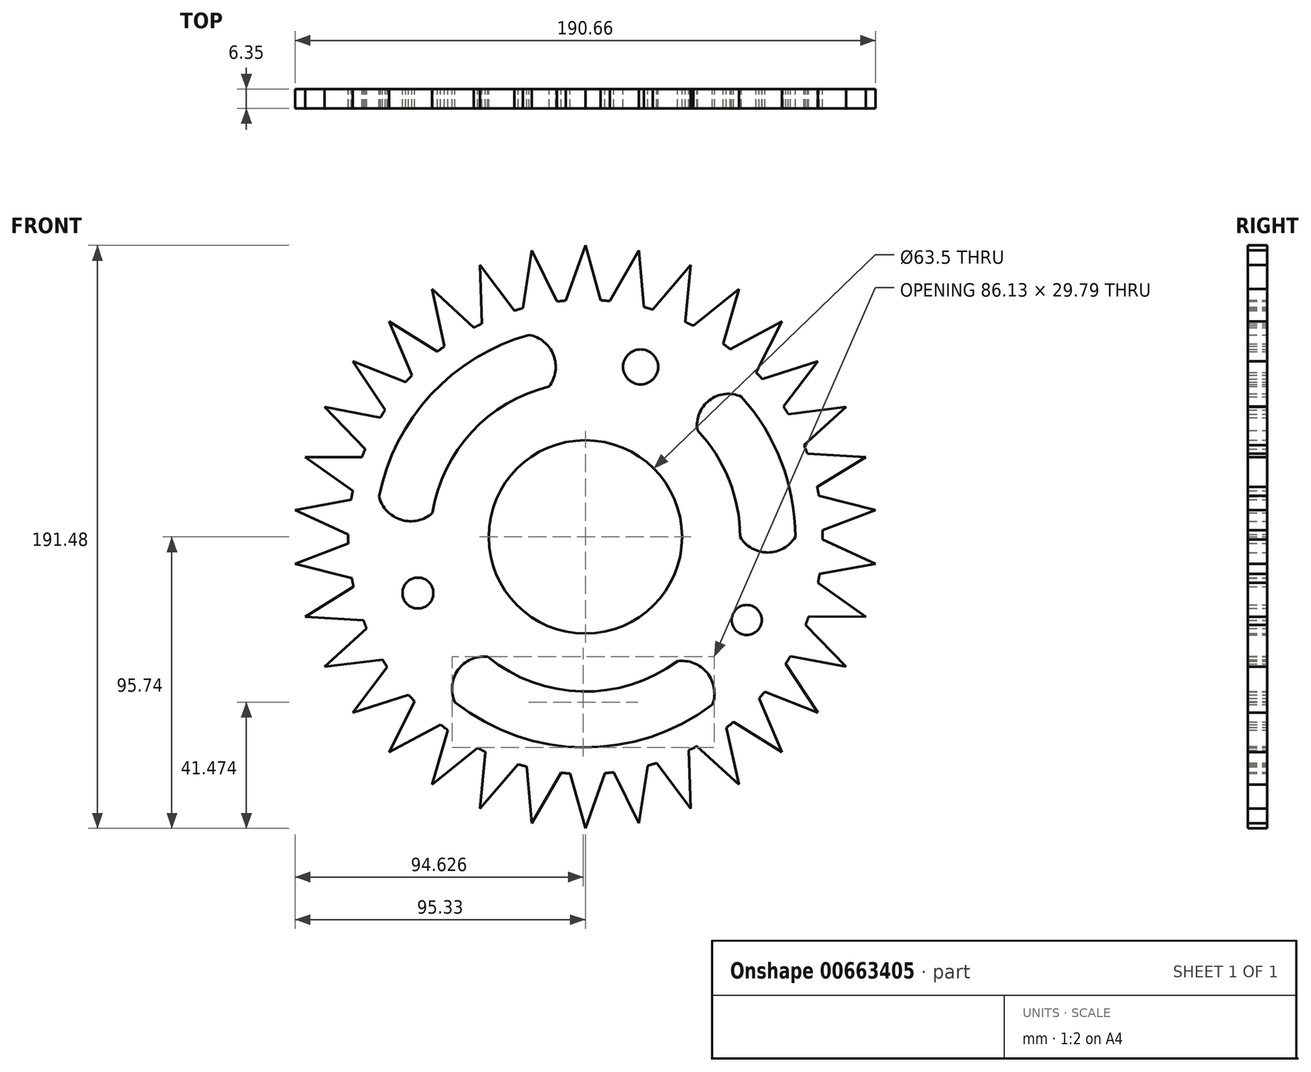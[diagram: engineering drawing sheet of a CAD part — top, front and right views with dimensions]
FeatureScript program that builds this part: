
annotation { "Feature Type Name" : "Feature", "Feature Type Description" : "" }
export const myFeature = defineFeature(function(context is Context, id is Id, definition is map)
    precondition{}
    {
        {
            var Q0;
            Q0=qCreatedBy(makeId("Front.planeOp"),FACE);
            var sketch = newSketch(context, id + "F0", { "sketchPlane" : qUnion([Q0])});
            skPoint(sketch, "E0.center", {"position": v(-0.06, -0.14) * mm});
            skCircle(sketch, "E1", {"center": v(0, 0) * mm, "radius": 31.75 * mm});
            skCircle(sketch, "E2", {"center": v(0, 0) * mm, "radius": 50.8 * mm});
            skCircle(sketch, "E3", {"center": v(-0.06, -0.14) * mm, "radius": 69.02 * mm});
            skArc(sketch, "E4", {"start": v(-67.78, 13.19) * mm, "mid": v(-60.47, 5.6) * mm, "end": v(-50.18, 7.9) * mm});
            skArc(sketch, "E5", {"start": v(-11.93, 49.38) * mm, "mid": v(-10.47, 59.73) * mm, "end": v(-18.54, 66.36) * mm});
            skArc(sketch, "E6", {"start": v(51.22, 46.07) * mm, "mid": v(40.68, 44.87) * mm, "end": v(36.82, 35) * mm});
            skArc(sketch, "E7", {"start": v(50.8, 0) * mm, "mid": v(59.88, -5.13) * mm, "end": v(68.97, 0) * mm});
            skArc(sketch, "E8", {"start": v(41.77, -55.05) * mm, "mid": v(40.02, -44.67) * mm, "end": v(30.22, -40.83) * mm});
            skArc(sketch, "E9", {"start": v(-32.1, -39.37) * mm, "mid": v(-41.83, -43.7) * mm, "end": v(-42.85, -54.3) * mm});
            skCircle(sketch, "E10", {"center": v(18.14, 55.84) * mm, "radius": 5.75 * mm});
            skCircle(sketch, "E11", {"center": v(53, -27.3) * mm, "radius": 4.93 * mm});
            skCircle(sketch, "E12", {"center": v(-55, -18.45) * mm, "radius": 5.06 * mm});
            skCircle(sketch, "E13", {"center": v(0, 0) * mm, "radius": 77.89 * mm});
            skLineSegment(sketch, "E14", {"start": v(-6.39, 77.63) * mm, "end": v(0, 95.74) * mm});
            skLineSegment(sketch, "E15", {"start": v(0, 95.74) * mm, "end": v(5.06, 77.72) * mm});
            skLineSegment(sketch, "E16.1.0", {"start": v(-20.54, 75.13) * mm, "end": v(-17.6, 94.11) * mm});
            skLineSegment(sketch, "E16.1.1", {"start": v(-17.6, 94.11) * mm, "end": v(-9.3, 77.33) * mm});
            skLineSegment(sketch, "E16.2.0", {"start": v(-34, 70.08) * mm, "end": v(-34.59, 89.28) * mm});
            skLineSegment(sketch, "E16.2.1", {"start": v(-34.59, 89.28) * mm, "end": v(-23.36, 74.3) * mm});
            skLineSegment(sketch, "E17.1.3.0", {"start": v(-46.3, 62.64) * mm, "end": v(-50.4, 81.4) * mm});
            skLineSegment(sketch, "E17.3.3.0", {"start": v(-50.4, 81.4) * mm, "end": v(-36.61, 68.75) * mm});
            skLineSegment(sketch, "E17.1.4.0", {"start": v(-57.02, 53.06) * mm, "end": v(-64.5, 70.75) * mm});
            skLineSegment(sketch, "E17.3.4.0", {"start": v(-64.5, 70.75) * mm, "end": v(-48.62, 60.85) * mm});
            skLineSegment(sketch, "E17.1.5.0", {"start": v(-65.8, 41.68) * mm, "end": v(-76.4, 57.7) * mm});
            skLineSegment(sketch, "E17.3.5.0", {"start": v(-76.4, 57.7) * mm, "end": v(-58.98, 50.88) * mm});
            skLineSegment(sketch, "E17.1.6.0", {"start": v(-72.33, 28.88) * mm, "end": v(-85.7, 42.68) * mm});
            skLineSegment(sketch, "E17.3.6.0", {"start": v(-85.7, 42.68) * mm, "end": v(-67.32, 39.17) * mm});
            skLineSegment(sketch, "E17.1.7.0", {"start": v(-76.41, 15.1) * mm, "end": v(-92.09, 26.2) * mm});
            skLineSegment(sketch, "E17.3.7.0", {"start": v(-92.09, 26.2) * mm, "end": v(-73.37, 26.14) * mm});
            skLineSegment(sketch, "E17.1.8.0", {"start": v(-77.88, 0.8) * mm, "end": v(-95.33, 8.83) * mm});
            skLineSegment(sketch, "E17.3.8.0", {"start": v(-95.33, 8.83) * mm, "end": v(-76.93, 12.2) * mm});
            skLineSegment(sketch, "E17.1.9.0", {"start": v(-76.7, -13.52) * mm, "end": v(-95.33, -8.83) * mm});
            skLineSegment(sketch, "E17.3.9.0", {"start": v(-95.33, -8.83) * mm, "end": v(-77.86, -2.13) * mm});
            skLineSegment(sketch, "E17.1.10.0", {"start": v(-72.91, -27.39) * mm, "end": v(-92.09, -26.2) * mm});
            skLineSegment(sketch, "E17.3.10.0", {"start": v(-92.09, -26.2) * mm, "end": v(-76.14, -16.4) * mm});
            skLineSegment(sketch, "E17.1.11.0", {"start": v(-66.64, -40.32) * mm, "end": v(-85.7, -42.68) * mm});
            skLineSegment(sketch, "E17.3.11.0", {"start": v(-85.7, -42.68) * mm, "end": v(-71.83, -30.11) * mm});
            skLineSegment(sketch, "E17.1.12.0", {"start": v(-58.1, -51.88) * mm, "end": v(-76.4, -57.7) * mm});
            skLineSegment(sketch, "E17.3.12.0", {"start": v(-76.4, -57.7) * mm, "end": v(-65.07, -42.8) * mm});
            skLineSegment(sketch, "E17.1.13.0", {"start": v(-47.58, -61.67) * mm, "end": v(-64.5, -70.75) * mm});
            skLineSegment(sketch, "E17.3.13.0", {"start": v(-64.5, -70.75) * mm, "end": v(-56.1, -54.03) * mm});
            skLineSegment(sketch, "E17.1.14.0", {"start": v(-35.44, -69.36) * mm, "end": v(-50.4, -81.4) * mm});
            skLineSegment(sketch, "E17.3.14.0", {"start": v(-50.4, -81.4) * mm, "end": v(-45.22, -63.42) * mm});
            skLineSegment(sketch, "E17.1.15.0", {"start": v(-22.09, -74.7) * mm, "end": v(-34.59, -89.28) * mm});
            skLineSegment(sketch, "E17.3.15.0", {"start": v(-34.59, -89.28) * mm, "end": v(-32.8, -70.65) * mm});
            skLineSegment(sketch, "E17.1.16.0", {"start": v(-7.99, -77.48) * mm, "end": v(-17.6, -94.11) * mm});
            skLineSegment(sketch, "E17.3.16.0", {"start": v(-17.6, -94.11) * mm, "end": v(-19.26, -75.47) * mm});
            skLineSegment(sketch, "E17.1.17.0", {"start": v(6.39, -77.63) * mm, "end": v(0, -95.74) * mm});
            skLineSegment(sketch, "E17.3.17.0", {"start": v(0, -95.74) * mm, "end": v(-5.06, -77.72) * mm});
            skLineSegment(sketch, "E17.1.18.0", {"start": v(20.54, -75.13) * mm, "end": v(17.6, -94.11) * mm});
            skLineSegment(sketch, "E17.3.18.0", {"start": v(17.6, -94.11) * mm, "end": v(9.3, -77.33) * mm});
            skLineSegment(sketch, "E17.1.19.0", {"start": v(34, -70.08) * mm, "end": v(34.59, -89.28) * mm});
            skLineSegment(sketch, "E17.3.19.0", {"start": v(34.59, -89.28) * mm, "end": v(23.36, -74.3) * mm});
            skLineSegment(sketch, "E17.1.20.0", {"start": v(46.3, -62.64) * mm, "end": v(50.4, -81.4) * mm});
            skLineSegment(sketch, "E17.3.20.0", {"start": v(50.4, -81.4) * mm, "end": v(36.61, -68.75) * mm});
            skLineSegment(sketch, "E17.1.21.0", {"start": v(57.02, -53.06) * mm, "end": v(64.5, -70.75) * mm});
            skLineSegment(sketch, "E17.3.21.0", {"start": v(64.5, -70.75) * mm, "end": v(48.62, -60.85) * mm});
            skLineSegment(sketch, "E17.1.22.0", {"start": v(65.8, -41.68) * mm, "end": v(76.4, -57.7) * mm});
            skLineSegment(sketch, "E17.3.22.0", {"start": v(76.4, -57.7) * mm, "end": v(58.98, -50.88) * mm});
            skLineSegment(sketch, "E17.1.23.0", {"start": v(72.33, -28.88) * mm, "end": v(85.7, -42.68) * mm});
            skLineSegment(sketch, "E17.3.23.0", {"start": v(85.7, -42.68) * mm, "end": v(67.32, -39.17) * mm});
            skLineSegment(sketch, "E17.1.24.0", {"start": v(76.41, -15.1) * mm, "end": v(92.09, -26.2) * mm});
            skLineSegment(sketch, "E17.3.24.0", {"start": v(92.09, -26.2) * mm, "end": v(73.37, -26.14) * mm});
            skLineSegment(sketch, "E17.1.25.0", {"start": v(77.88, -0.8) * mm, "end": v(95.33, -8.83) * mm});
            skLineSegment(sketch, "E17.3.25.0", {"start": v(95.33, -8.83) * mm, "end": v(76.93, -12.2) * mm});
            skLineSegment(sketch, "E17.1.26.0", {"start": v(76.7, 13.52) * mm, "end": v(95.33, 8.83) * mm});
            skLineSegment(sketch, "E17.3.26.0", {"start": v(95.33, 8.83) * mm, "end": v(77.86, 2.13) * mm});
            skLineSegment(sketch, "E17.1.27.0", {"start": v(72.91, 27.39) * mm, "end": v(92.09, 26.2) * mm});
            skLineSegment(sketch, "E17.3.27.0", {"start": v(92.09, 26.2) * mm, "end": v(76.14, 16.4) * mm});
            skLineSegment(sketch, "E17.1.28.0", {"start": v(66.64, 40.32) * mm, "end": v(85.7, 42.68) * mm});
            skLineSegment(sketch, "E17.3.28.0", {"start": v(85.7, 42.68) * mm, "end": v(71.83, 30.11) * mm});
            skLineSegment(sketch, "E17.1.29.0", {"start": v(58.1, 51.88) * mm, "end": v(76.4, 57.7) * mm});
            skLineSegment(sketch, "E17.3.29.0", {"start": v(76.4, 57.7) * mm, "end": v(65.07, 42.8) * mm});
            skLineSegment(sketch, "E18.1.30.0", {"start": v(47.58, 61.67) * mm, "end": v(64.5, 70.75) * mm});
            skLineSegment(sketch, "E18.3.30.0", {"start": v(64.5, 70.75) * mm, "end": v(56.1, 54.03) * mm});
            skLineSegment(sketch, "E18.1.31.0", {"start": v(35.44, 69.36) * mm, "end": v(50.4, 81.4) * mm});
            skLineSegment(sketch, "E18.3.31.0", {"start": v(50.4, 81.4) * mm, "end": v(45.22, 63.42) * mm});
            skLineSegment(sketch, "E18.1.32.0", {"start": v(22.09, 74.7) * mm, "end": v(34.59, 89.28) * mm});
            skLineSegment(sketch, "E18.3.32.0", {"start": v(34.59, 89.28) * mm, "end": v(32.8, 70.65) * mm});
            skLineSegment(sketch, "E18.1.33.0", {"start": v(7.99, 77.48) * mm, "end": v(17.6, 94.11) * mm});
            skLineSegment(sketch, "E18.3.33.0", {"start": v(17.6, 94.11) * mm, "end": v(19.26, 75.47) * mm});
            skSolve(sketch);
        }
        {
            var Q0;
            {var subQ5=sQuery(id+"F0.wireOp",EDGE,"3mBp1R15-14Ga-4iic-g8rZ-xZIpD9eXclui");var subQ7=makeQuery(id+"F0.imprint","INTERSECT",VERTEX,{"derivedFrom":[subQ5,sQuery(id+"F0.wireOp",EDGE,"E0.2.1")]});Q0=makeQuery(id+"F0.imprint","IMPRINT",FACE,{"disambiguationData":[TD([[makeQuery(id+"F0.imprint","IMPRINT",EDGE,{"disambiguationData":[TD([[subQ7,-1.0]])],"derivedFrom":subQ5}),1.0]])]});}
            var Q1;
            Q1=makeQuery(id+"F0.imprint","IMPRINT",FACE,{"disambiguationData":[TD([[makeQuery(id+"F0.imprint","IMPRINT",EDGE,{"derivedFrom":sQuery(id+"F0.wireOp",EDGE,"E1")}),-1.0]])]});
            var Q2;
            {var subQ0=sQuery(id+"F0.wireOp",EDGE,"E7");Q2=makeQuery(id+"F0.imprint","IMPRINT",FACE,{"disambiguationData":[TD([[makeQuery(id+"F0.imprint","IMPRINT",EDGE,{"derivedFrom":subQ0}),-1.0]])]});}
            var Q3;
            {var subQ0=sQuery(id+"F0.wireOp",EDGE,"E4");Q3=makeQuery(id+"F0.imprint","IMPRINT",FACE,{"disambiguationData":[TD([[makeQuery(id+"F0.imprint","IMPRINT",EDGE,{"derivedFrom":subQ0}),-1.0]])]});}
            var Q4;
            {var subQ0=sQuery(id+"F0.wireOp",EDGE,"E5");Q4=makeQuery(id+"F0.imprint","IMPRINT",FACE,{"disambiguationData":[TD([[makeQuery(id+"F0.imprint","IMPRINT",EDGE,{"derivedFrom":subQ0}),-1.0]])]});}
            var Q5;
            {var subQ0=sQuery(id+"F0.wireOp",EDGE,"E0.2.1");Q5=makeQuery(id+"F0.imprint","IMPRINT",FACE,{"disambiguationData":[TD([[makeQuery(id+"F0.imprint","IMPRINT",EDGE,{"derivedFrom":subQ0}),-1.0]])]});}
            var Q6;
            {var subQ0=sQuery(id+"F0.wireOp",EDGE,"qIJbHyuC-GWzO-xRoJ-OiaV-YKGvx3o68cOa");Q6=makeQuery(id+"F0.imprint","IMPRINT",FACE,{"disambiguationData":[TD([[makeQuery(id+"F0.imprint","IMPRINT",EDGE,{"derivedFrom":subQ0}),-1.0]])]});}
            var Q7;
            {var subQ0=sQuery(id+"F0.wireOp",EDGE,"E0.1.1");var subQ1=sQuery(id+"F0.wireOp",EDGE,"3mBp1R15-14Ga-4iic-g8rZ-xZIpD9eXclui");var subQ2=makeQuery(id+"F0.imprint","INTERSECT",VERTEX,{"derivedFrom":[subQ1,subQ0]});Q7=makeQuery(id+"F0.imprint","IMPRINT",FACE,{"disambiguationData":[TD([[makeQuery(id+"F0.imprint","IMPRINT",EDGE,{"disambiguationData":[TD([[subQ2,-1.0]])],"derivedFrom":subQ1}),-1.0]])]});}
            var Q8;
            {var subQ0=sQuery(id+"F0.wireOp",EDGE,"E16.1.0");Q8=makeQuery(id+"F0.imprint","IMPRINT",FACE,{"disambiguationData":[TD([[makeQuery(id+"F0.imprint","IMPRINT",EDGE,{"derivedFrom":subQ0}),-1.0]])]});}
            var Q9;
            {var subQ0=sQuery(id+"F0.wireOp",EDGE,"E14");Q9=makeQuery(id+"F0.imprint","IMPRINT",FACE,{"disambiguationData":[TD([[makeQuery(id+"F0.imprint","IMPRINT",EDGE,{"derivedFrom":subQ0}),-1.0]])]});}
            var Q10;
            {var subQ0=sQuery(id+"F0.wireOp",EDGE,"E18.1.33.0");Q10=makeQuery(id+"F0.imprint","IMPRINT",FACE,{"disambiguationData":[TD([[makeQuery(id+"F0.imprint","IMPRINT",EDGE,{"derivedFrom":subQ0}),-1.0]])]});}
            var Q11;
            {var subQ0=sQuery(id+"F0.wireOp",EDGE,"E18.1.32.0");Q11=makeQuery(id+"F0.imprint","IMPRINT",FACE,{"disambiguationData":[TD([[makeQuery(id+"F0.imprint","IMPRINT",EDGE,{"derivedFrom":subQ0}),-1.0]])]});}
            var Q12;
            {var subQ0=sQuery(id+"F0.wireOp",EDGE,"E17.1.9.0");Q12=makeQuery(id+"F0.imprint","IMPRINT",FACE,{"disambiguationData":[TD([[makeQuery(id+"F0.imprint","IMPRINT",EDGE,{"derivedFrom":subQ0}),-1.0]])]});}
            var Q13;
            {var subQ0=sQuery(id+"F0.wireOp",EDGE,"E17.1.8.0");Q13=makeQuery(id+"F0.imprint","IMPRINT",FACE,{"disambiguationData":[TD([[makeQuery(id+"F0.imprint","IMPRINT",EDGE,{"derivedFrom":subQ0}),-1.0]])]});}
            var Q14;
            {var subQ0=sQuery(id+"F0.wireOp",EDGE,"E17.1.7.0");Q14=makeQuery(id+"F0.imprint","IMPRINT",FACE,{"disambiguationData":[TD([[makeQuery(id+"F0.imprint","IMPRINT",EDGE,{"derivedFrom":subQ0}),-1.0]])]});}
            var Q15;
            {var subQ0=sQuery(id+"F0.wireOp",EDGE,"E17.1.6.0");Q15=makeQuery(id+"F0.imprint","IMPRINT",FACE,{"disambiguationData":[TD([[makeQuery(id+"F0.imprint","IMPRINT",EDGE,{"derivedFrom":subQ0}),-1.0]])]});}
            var Q16;
            {var subQ0=sQuery(id+"F0.wireOp",EDGE,"E17.1.5.0");Q16=makeQuery(id+"F0.imprint","IMPRINT",FACE,{"disambiguationData":[TD([[makeQuery(id+"F0.imprint","IMPRINT",EDGE,{"derivedFrom":subQ0}),-1.0]])]});}
            var Q17;
            {var subQ0=sQuery(id+"F0.wireOp",EDGE,"E17.1.4.0");Q17=makeQuery(id+"F0.imprint","IMPRINT",FACE,{"disambiguationData":[TD([[makeQuery(id+"F0.imprint","IMPRINT",EDGE,{"derivedFrom":subQ0}),-1.0]])]});}
            var Q18;
            {var subQ0=sQuery(id+"F0.wireOp",EDGE,"E17.1.3.0");Q18=makeQuery(id+"F0.imprint","IMPRINT",FACE,{"disambiguationData":[TD([[makeQuery(id+"F0.imprint","IMPRINT",EDGE,{"derivedFrom":subQ0}),-1.0]])]});}
            var Q19;
            {var subQ0=sQuery(id+"F0.wireOp",EDGE,"E16.2.0");Q19=makeQuery(id+"F0.imprint","IMPRINT",FACE,{"disambiguationData":[TD([[makeQuery(id+"F0.imprint","IMPRINT",EDGE,{"derivedFrom":subQ0}),-1.0]])]});}
            var Q20;
            {var subQ0=sQuery(id+"F0.wireOp",EDGE,"E18.1.31.0");Q20=makeQuery(id+"F0.imprint","IMPRINT",FACE,{"disambiguationData":[TD([[makeQuery(id+"F0.imprint","IMPRINT",EDGE,{"derivedFrom":subQ0}),-1.0]])]});}
            var Q21;
            {var subQ0=sQuery(id+"F0.wireOp",EDGE,"E18.1.30.0");Q21=makeQuery(id+"F0.imprint","IMPRINT",FACE,{"disambiguationData":[TD([[makeQuery(id+"F0.imprint","IMPRINT",EDGE,{"derivedFrom":subQ0}),-1.0]])]});}
            var Q22;
            {var subQ0=sQuery(id+"F0.wireOp",EDGE,"E17.1.29.0");Q22=makeQuery(id+"F0.imprint","IMPRINT",FACE,{"disambiguationData":[TD([[makeQuery(id+"F0.imprint","IMPRINT",EDGE,{"derivedFrom":subQ0}),-1.0]])]});}
            var Q23;
            {var subQ0=sQuery(id+"F0.wireOp",EDGE,"E17.1.28.0");Q23=makeQuery(id+"F0.imprint","IMPRINT",FACE,{"disambiguationData":[TD([[makeQuery(id+"F0.imprint","IMPRINT",EDGE,{"derivedFrom":subQ0}),-1.0]])]});}
            var Q24;
            {var subQ0=sQuery(id+"F0.wireOp",EDGE,"E17.1.27.0");Q24=makeQuery(id+"F0.imprint","IMPRINT",FACE,{"disambiguationData":[TD([[makeQuery(id+"F0.imprint","IMPRINT",EDGE,{"derivedFrom":subQ0}),-1.0]])]});}
            var Q25;
            {var subQ0=sQuery(id+"F0.wireOp",EDGE,"E17.1.26.0");Q25=makeQuery(id+"F0.imprint","IMPRINT",FACE,{"disambiguationData":[TD([[makeQuery(id+"F0.imprint","IMPRINT",EDGE,{"derivedFrom":subQ0}),-1.0]])]});}
            var Q26;
            {var subQ0=sQuery(id+"F0.wireOp",EDGE,"E17.1.25.0");Q26=makeQuery(id+"F0.imprint","IMPRINT",FACE,{"disambiguationData":[TD([[makeQuery(id+"F0.imprint","IMPRINT",EDGE,{"derivedFrom":subQ0}),-1.0]])]});}
            var Q27;
            {var subQ0=sQuery(id+"F0.wireOp",EDGE,"E17.1.23.0");Q27=makeQuery(id+"F0.imprint","IMPRINT",FACE,{"disambiguationData":[TD([[makeQuery(id+"F0.imprint","IMPRINT",EDGE,{"derivedFrom":subQ0}),-1.0]])]});}
            var Q28;
            {var subQ0=sQuery(id+"F0.wireOp",EDGE,"E17.1.24.0");Q28=makeQuery(id+"F0.imprint","IMPRINT",FACE,{"disambiguationData":[TD([[makeQuery(id+"F0.imprint","IMPRINT",EDGE,{"derivedFrom":subQ0}),-1.0]])]});}
            var Q29;
            {var subQ0=sQuery(id+"F0.wireOp",EDGE,"E17.1.22.0");Q29=makeQuery(id+"F0.imprint","IMPRINT",FACE,{"disambiguationData":[TD([[makeQuery(id+"F0.imprint","IMPRINT",EDGE,{"derivedFrom":subQ0}),-1.0]])]});}
            var Q30;
            {var subQ0=sQuery(id+"F0.wireOp",EDGE,"E17.1.21.0");Q30=makeQuery(id+"F0.imprint","IMPRINT",FACE,{"disambiguationData":[TD([[makeQuery(id+"F0.imprint","IMPRINT",EDGE,{"derivedFrom":subQ0}),-1.0]])]});}
            var Q31;
            {var subQ0=sQuery(id+"F0.wireOp",EDGE,"E17.1.19.0");Q31=makeQuery(id+"F0.imprint","IMPRINT",FACE,{"disambiguationData":[TD([[makeQuery(id+"F0.imprint","IMPRINT",EDGE,{"derivedFrom":subQ0}),-1.0]])]});}
            var Q32;
            {var subQ0=sQuery(id+"F0.wireOp",EDGE,"E17.1.18.0");Q32=makeQuery(id+"F0.imprint","IMPRINT",FACE,{"disambiguationData":[TD([[makeQuery(id+"F0.imprint","IMPRINT",EDGE,{"derivedFrom":subQ0}),-1.0]])]});}
            var Q33;
            {var subQ0=sQuery(id+"F0.wireOp",EDGE,"E17.1.17.0");Q33=makeQuery(id+"F0.imprint","IMPRINT",FACE,{"disambiguationData":[TD([[makeQuery(id+"F0.imprint","IMPRINT",EDGE,{"derivedFrom":subQ0}),-1.0]])]});}
            var Q34;
            {var subQ0=sQuery(id+"F0.wireOp",EDGE,"E17.1.15.0");Q34=makeQuery(id+"F0.imprint","IMPRINT",FACE,{"disambiguationData":[TD([[makeQuery(id+"F0.imprint","IMPRINT",EDGE,{"derivedFrom":subQ0}),-1.0]])]});}
            var Q35;
            {var subQ0=sQuery(id+"F0.wireOp",EDGE,"E17.1.14.0");Q35=makeQuery(id+"F0.imprint","IMPRINT",FACE,{"disambiguationData":[TD([[makeQuery(id+"F0.imprint","IMPRINT",EDGE,{"derivedFrom":subQ0}),-1.0]])]});}
            var Q36;
            {var subQ0=sQuery(id+"F0.wireOp",EDGE,"E17.1.13.0");Q36=makeQuery(id+"F0.imprint","IMPRINT",FACE,{"disambiguationData":[TD([[makeQuery(id+"F0.imprint","IMPRINT",EDGE,{"derivedFrom":subQ0}),-1.0]])]});}
            var Q37;
            {var subQ0=sQuery(id+"F0.wireOp",EDGE,"E17.1.10.0");Q37=makeQuery(id+"F0.imprint","IMPRINT",FACE,{"disambiguationData":[TD([[makeQuery(id+"F0.imprint","IMPRINT",EDGE,{"derivedFrom":subQ0}),-1.0]])]});}
            var Q38;
            {var subQ26=sQuery(id+"F0.wireOp",EDGE,"E3");var subQ36=makeQuery(id+"F0.imprint","INTERSECT",VERTEX,{"derivedFrom":[subQ26,sQuery(id+"F0.wireOp",EDGE,"E6")]});Q38=makeQuery(id+"F0.imprint","IMPRINT",FACE,{"disambiguationData":[TD([[makeQuery(id+"F0.imprint","IMPRINT",EDGE,{"disambiguationData":[TD([[subQ36,1.0]])],"derivedFrom":subQ26}),-1.0]])]});}
            var Q39;
            {var subQ0=sQuery(id+"F0.wireOp",EDGE,"E17.1.20.0");Q39=makeQuery(id+"F0.imprint","IMPRINT",FACE,{"disambiguationData":[TD([[makeQuery(id+"F0.imprint","IMPRINT",EDGE,{"derivedFrom":subQ0}),-1.0]])]});}
            var Q40;
            {var subQ0=sQuery(id+"F0.wireOp",EDGE,"E17.1.16.0");Q40=makeQuery(id+"F0.imprint","IMPRINT",FACE,{"disambiguationData":[TD([[makeQuery(id+"F0.imprint","IMPRINT",EDGE,{"derivedFrom":subQ0}),-1.0]])]});}
            var Q41;
            {var subQ0=sQuery(id+"F0.wireOp",EDGE,"E17.1.12.0");Q41=makeQuery(id+"F0.imprint","IMPRINT",FACE,{"disambiguationData":[TD([[makeQuery(id+"F0.imprint","IMPRINT",EDGE,{"derivedFrom":subQ0}),-1.0]])]});}
            var Q42;
            {var subQ0=sQuery(id+"F0.wireOp",EDGE,"E17.1.11.0");Q42=makeQuery(id+"F0.imprint","IMPRINT",FACE,{"disambiguationData":[TD([[makeQuery(id+"F0.imprint","IMPRINT",EDGE,{"derivedFrom":subQ0}),-1.0]])]});}
            extrude(context, id + "F1", {"entities" : qUnion([Q0, Q1, Q2, Q3, Q4, Q5, Q6, Q7, Q8, Q9, Q10, Q11, Q12, Q13, Q14, Q15, Q16, Q17, Q18, Q19, Q20, Q21, Q22, Q23, Q24, Q25, Q26, Q27, Q28, Q29, Q30, Q31, Q32, Q33, Q34, Q35, Q36, Q37, Q38, Q39, Q40, Q41, Q42]), "depth" : 6.35 * mm, "offsetDistance" : 25.4 * mm});
        }
    });
